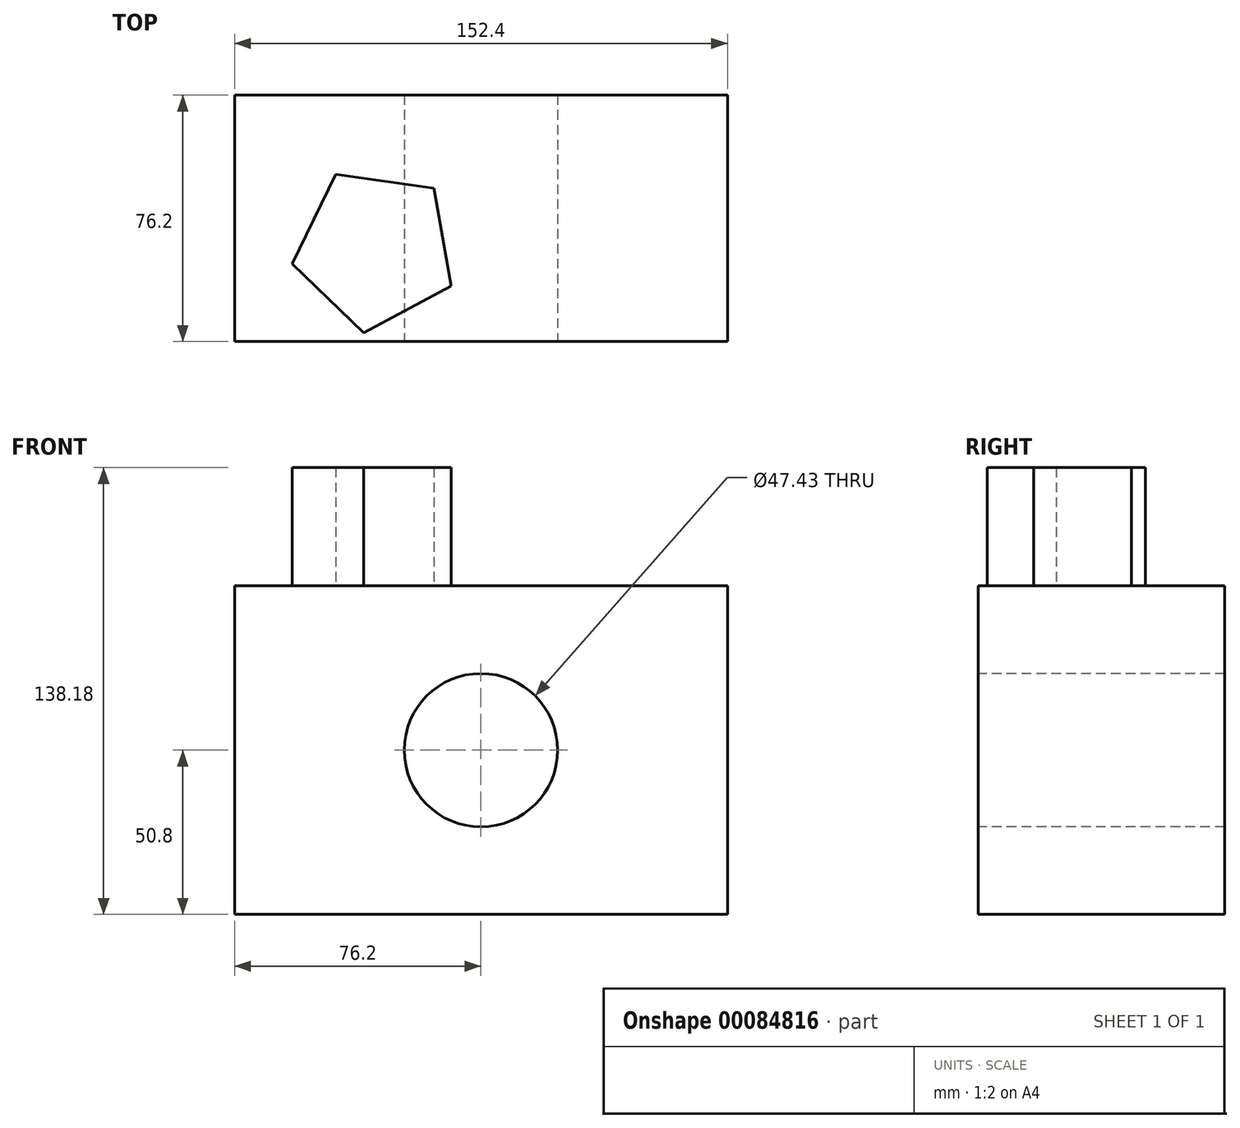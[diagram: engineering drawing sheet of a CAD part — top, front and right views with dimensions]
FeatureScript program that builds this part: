
annotation { "Feature Type Name" : "Feature", "Feature Type Description" : "" }
export const myFeature = defineFeature(function(context is Context, id is Id, definition is map)
    precondition{}
    {
        {
            var Q0;
            Q0=qCreatedBy(makeId("Front.planeOp"),FACE);
            var sketch = newSketch(context, id + "F0", { "sketchPlane" : qUnion([Q0])});
            skLineSegment(sketch, "E0.bottom", {"start": v(-76.2, 50.8) * mm, "end": v(76.2, 50.8) * mm});
            skLineSegment(sketch, "E0.top", {"start": v(-76.2, -50.8) * mm, "end": v(76.2, -50.8) * mm});
            skLineSegment(sketch, "E0.left", {"start": v(-76.2, 50.8) * mm, "end": v(-76.2, -50.8) * mm});
            skLineSegment(sketch, "E0.right", {"start": v(76.2, 50.8) * mm, "end": v(76.2, -50.8) * mm});
            skPoint(sketch, "E0.middle", {"position": v(0, 0) * mm});
            skSolve(sketch);
        }
        {
            var Q0;
            Q0=makeQuery(id+"F0.imprint","IMPRINT",FACE,{"disambiguationData":[TD([[makeQuery(id+"F0.imprint","IMPRINT",EDGE,{"derivedFrom":sQuery(id+"F0.wireOp",EDGE,"E0.bottom")}),-1.0]])]});
            extrude(context, id + "F1", {"entities" : qUnion([Q0]), "depth" : 76.2 * mm});
        }
        {
            var Q0;
            Q0=makeQuery(id+"F1.opExtrude","CAP_FACE",FACE,{"disambiguationData":[OSD([sQuery(id+"F0.wireOp",EDGE,"E0.bottom"),sQuery(id+"F0.wireOp",EDGE,"E0.top"),sQuery(id+"F0.wireOp",EDGE,"E0.left"),sQuery(id+"F0.wireOp",EDGE,"E0.right")])],"isStart":false});
            var sketch = newSketch(context, id + "F2", { "sketchPlane" : qUnion([Q0])});
            skCircle(sketch, "E1", {"center": v(0, 0) * mm, "radius": 23.72 * mm});
            skSolve(sketch);
        }
        {
            var Q0;
            Q0=makeQuery(id+"F2.imprint","IMPRINT",FACE,{"disambiguationData":[TD([[makeQuery(id+"F2.imprint","IMPRINT",EDGE,{"derivedFrom":sQuery(id+"F2.wireOp",EDGE,"E1")}),1.0]])]});
            extrude(context, id + "F3", {"entities" : qUnion([Q0]), "operationType" : NewBodyOperationType.REMOVE, "endBound" : BoundingType.THROUGH_ALL, "oppositeDirection" : true, "depth" : 96.76 * mm});
        }
        {
            var Q0;
            Q0=makeQuery(id+"F1.opExtrude","SWEPT_FACE",FACE,{"disambiguationData":[OSD([sQuery(id+"F0.wireOp",EDGE,"E0.bottom")])]});
            var sketch = newSketch(context, id + "F4", { "sketchPlane" : qUnion([Q0])});
            skCircle(sketch, "E2.cCircle", {"center": v(-32.66, -47.6) * mm, "radius": 26.12 * mm, "construction": true});
            skLineSegment(sketch, "E2.0", {"start": v(-44.9, -24.52) * mm, "end": v(-14.5, -28.82) * mm});
            skLineSegment(sketch, "E2.1", {"start": v(-14.5, -28.82) * mm, "end": v(-9.2, -59.06) * mm});
            skLineSegment(sketch, "E2.2", {"start": v(-9.2, -59.06) * mm, "end": v(-36.31, -73.45) * mm});
            skLineSegment(sketch, "E2.3", {"start": v(-36.31, -73.45) * mm, "end": v(-58.38, -52.1) * mm});
            skLineSegment(sketch, "E2.4", {"start": v(-58.38, -52.1) * mm, "end": v(-44.9, -24.52) * mm});
            skSolve(sketch);
        }
        {
            var Q0;
            Q0 = qSketchRegion(id + "F4", true);
            extrude(context, id + "F5", {"entities" : qUnion([Q0]), "operationType" : NewBodyOperationType.ADD, "depth" : 36.58 * mm});
        }
    });
